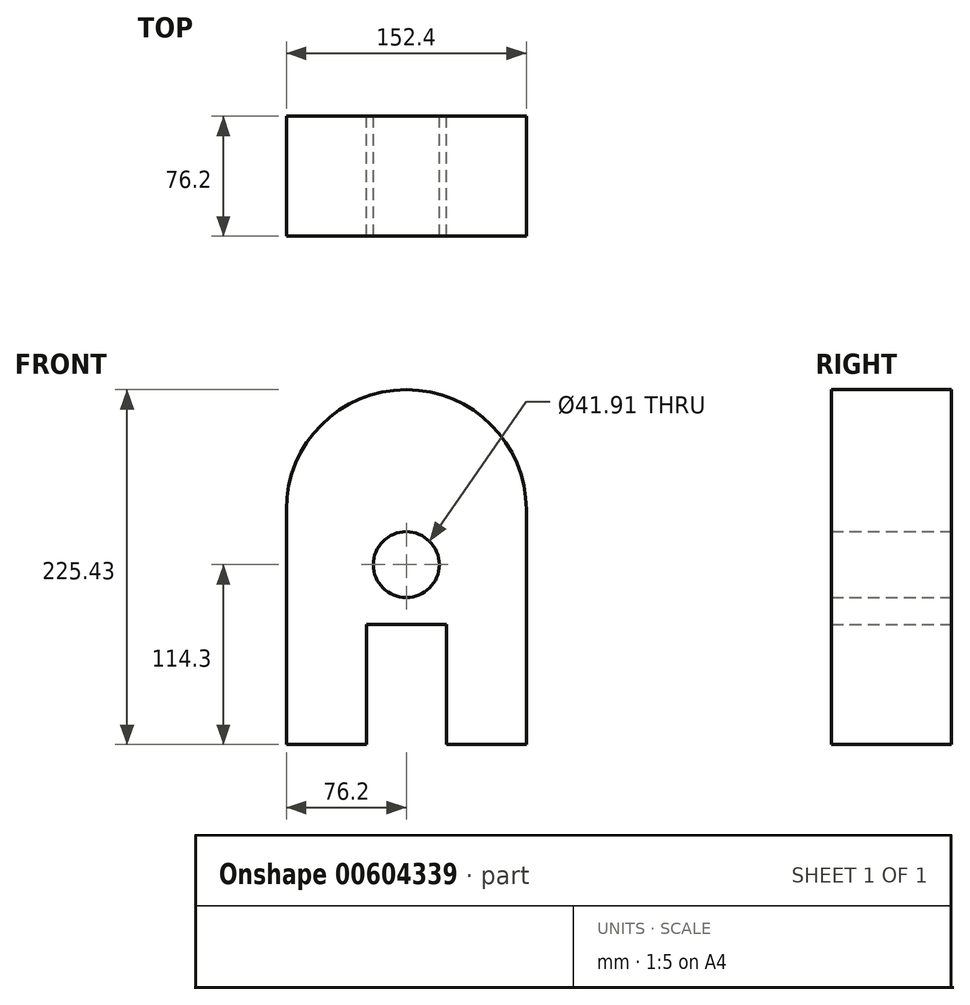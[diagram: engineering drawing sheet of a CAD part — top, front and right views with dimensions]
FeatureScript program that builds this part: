
annotation { "Feature Type Name" : "Feature", "Feature Type Description" : "" }
export const myFeature = defineFeature(function(context is Context, id is Id, definition is map)
    precondition{}
    {
        {
            var Q0;
            Q0=qCreatedBy(makeId("Front.planeOp"),FACE);
            var sketch = newSketch(context, id + "F0", { "sketchPlane" : qUnion([Q0])});
            skLineSegment(sketch, "E0", {"start": v(0, 0) * mm, "end": v(50.8, 0) * mm});
            skLineSegment(sketch, "E1", {"start": v(50.8, 0) * mm, "end": v(50.8, 76.2) * mm});
            skLineSegment(sketch, "E2", {"start": v(50.8, 76.2) * mm, "end": v(101.6, 76.2) * mm});
            skLineSegment(sketch, "E3", {"start": v(101.6, 76.2) * mm, "end": v(101.6, 0) * mm});
            skLineSegment(sketch, "E4", {"start": v(101.6, 0) * mm, "end": v(152.4, 0) * mm});
            skLineSegment(sketch, "E5", {"start": v(152.4, 0) * mm, "end": v(152.4, 149.23) * mm});
            skLineSegment(sketch, "E6", {"start": v(0, 0) * mm, "end": v(0, 149.23) * mm});
            skArc(sketch, "E7", {"start": v(152.4, 149.23) * mm, "mid": v(76.2, 225.43) * mm, "end": v(0, 149.23) * mm});
            skCircle(sketch, "E8", {"center": v(76.2, 114.3) * mm, "radius": 20.96 * mm});
            skSolve(sketch);
        }
        {
            var Q0;
            Q0=makeQuery(id+"F0.imprint","IMPRINT",FACE,{"disambiguationData":[TD([[makeQuery(id+"F0.imprint","IMPRINT",EDGE,{"derivedFrom":sQuery(id+"F0.wireOp",EDGE,"E0")}),1.0]])]});
            extrude(context, id + "F1", {"entities" : qUnion([Q0]), "depth" : 76.2 * mm, "offsetDistance" : 25.4 * mm});
        }
    });
